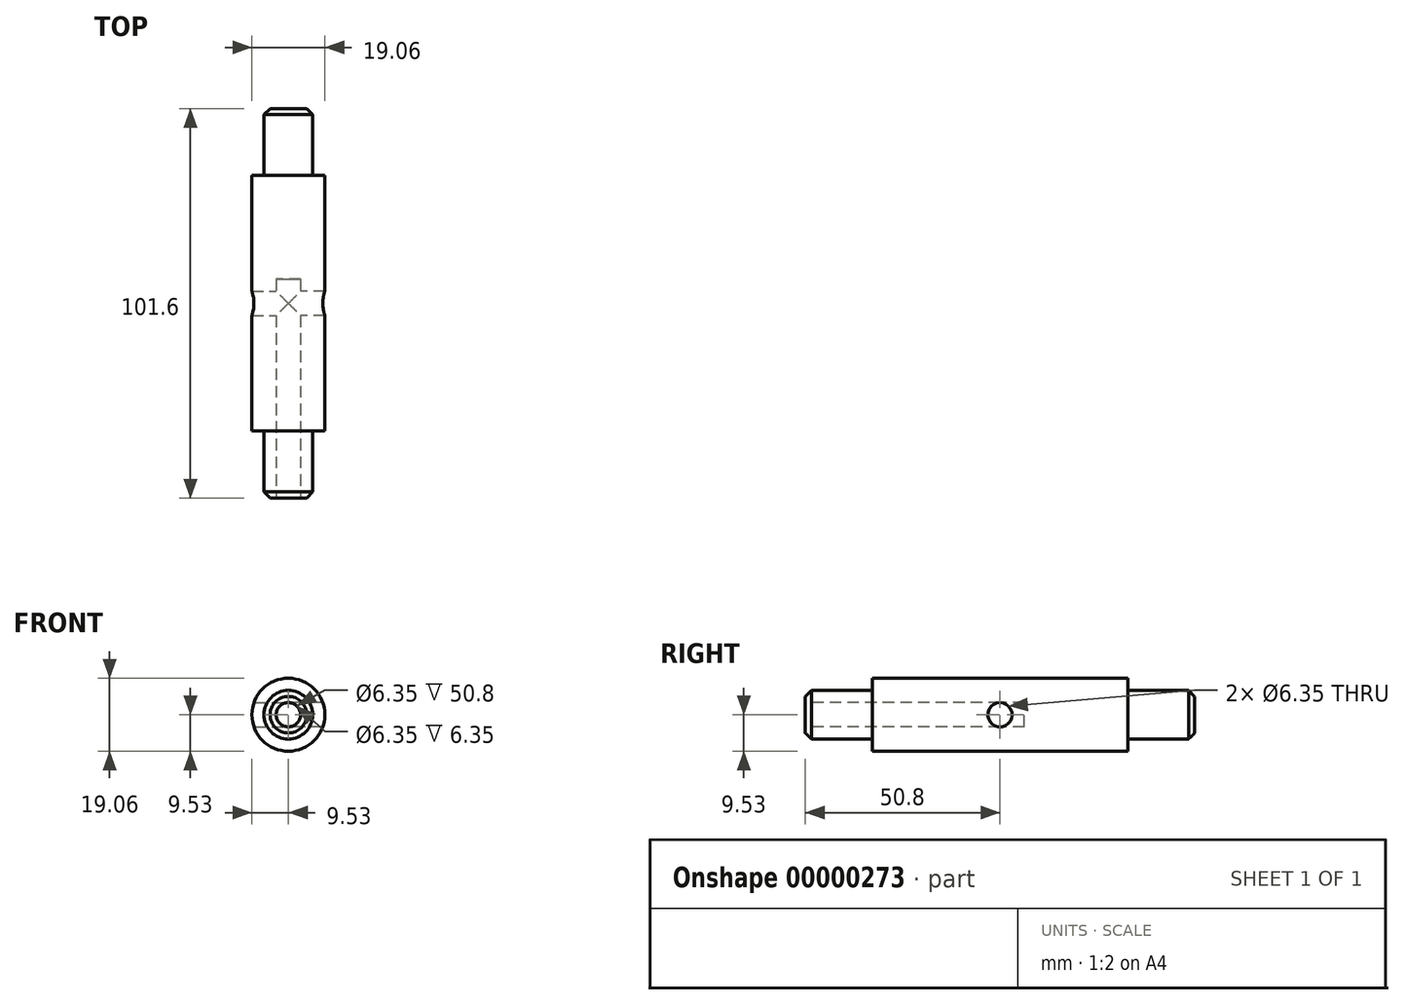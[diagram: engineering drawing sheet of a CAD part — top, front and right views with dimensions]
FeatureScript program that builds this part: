
annotation { "Feature Type Name" : "Feature", "Feature Type Description" : "" }
export const myFeature = defineFeature(function(context is Context, id is Id, definition is map)
    precondition{}
    {
        {
            var Q0;
            Q0=qCreatedBy(makeId("Front.planeOp"),FACE);
            var sketch = newSketch(context, id + "F0", { "sketchPlane" : qUnion([Q0])});
            skCircle(sketch, "E0", {"center": v(0, 0) * mm, "radius": 6.35 * mm});
            skSolve(sketch);
        }
        {
            var Q0;
            Q0=makeQuery(id+"F0.imprint","IMPRINT",FACE,{"disambiguationData":[TD([[makeQuery(id+"F0.imprint","IMPRINT",EDGE,{"derivedFrom":sQuery(id+"F0.wireOp",EDGE,"E0")}),1.0]])]});
            extrude(context, id + "F1", {"entities" : qUnion([Q0]), "depth" : 17.46 * mm});
        }
        {
            var Q0;
            Q0=makeQuery(id+"F1.opExtrude","CAP_FACE",FACE,{"disambiguationData":[OSD([sQuery(id+"F0.wireOp",EDGE,"E0")])],"isStart":false});
            var sketch = newSketch(context, id + "F2", { "sketchPlane" : qUnion([Q0])});
            skCircle(sketch, "E1", {"center": v(0, 0) * mm, "radius": 9.53 * mm});
            skSolve(sketch);
        }
        {
            var Q0;
            {var subQ0=makeQuery(id+"F2.imprint","IMPRINT",EDGE,{"derivedFrom":makeQuery(id+"F1.opExtrude","CAP_EDGE",EDGE,{"disambiguationData":[OSD([sQuery(id+"F0.wireOp",EDGE,"E0")])],"isStart":false})});Q0=qUnion([makeQuery(id+"F2.imprint","IMPRINT",FACE,{"disambiguationData":[TD([[makeQuery(id+"F2.imprint","IMPRINT",EDGE,{"derivedFrom":sQuery(id+"F2.wireOp",EDGE,"E1")}),1.0]])]}),makeQuery(id+"F2.imprint","IMPRINT",FACE,{"disambiguationData":[TD([[subQ0,1.0]])]})]);}
            extrude(context, id + "F3", {"entities" : qUnion([Q0]), "operationType" : NewBodyOperationType.ADD, "depth" : 66.67 * mm});
        }
        {
            var Q0;
            Q0=makeQuery(id+"F3.opExtrude","CAP_FACE",FACE,{"disambiguationData":[OSD([sQuery(id+"F2.wireOp",EDGE,"E1")])],"isStart":false});
            var sketch = newSketch(context, id + "F4", { "sketchPlane" : qUnion([Q0])});
            skCircle(sketch, "E2", {"center": v(0, 0) * mm, "radius": 6.35 * mm});
            skSolve(sketch);
        }
        {
            var Q0;
            Q0=makeQuery(id+"F4.imprint","IMPRINT",FACE,{"disambiguationData":[TD([[makeQuery(id+"F4.imprint","IMPRINT",EDGE,{"derivedFrom":sQuery(id+"F4.wireOp",EDGE,"E2")}),1.0]])]});
            extrude(context, id + "F5", {"entities" : qUnion([Q0]), "operationType" : NewBodyOperationType.ADD, "depth" : 17.46 * mm});
        }
        {
            var Q0;
            Q0=makeQuery(id+"F5.opExtrude","CAP_EDGE",EDGE,{"disambiguationData":[OSD([sQuery(id+"F4.wireOp",EDGE,"E2")])],"isStart":false});
            var Q1;
            Q1=makeQuery(id+"F1.opExtrude","CAP_EDGE",EDGE,{"disambiguationData":[OSD([sQuery(id+"F0.wireOp",EDGE,"E0")])],"isStart":true});
            chamfer(context, id + "F6", {"entities" : qUnion([Q0, Q1]), "width" : 1.59 * mm, "tangentPropagation" : true});
        }
        {
            var Q0;
            Q0=makeQuery(id+"F5.opExtrude","CAP_FACE",FACE,{"disambiguationData":[OSD([sQuery(id+"F4.wireOp",EDGE,"E2")])],"isStart":false});
            var sketch = newSketch(context, id + "F7", { "sketchPlane" : qUnion([Q0])});
            skCircle(sketch, "E3", {"center": v(0, 0) * mm, "radius": 3.18 * mm});
            skSolve(sketch);
        }
        {
            var Q0;
            Q0=makeQuery(id+"F7.imprint","IMPRINT",FACE,{"disambiguationData":[TD([[makeQuery(id+"F7.imprint","IMPRINT",EDGE,{"derivedFrom":sQuery(id+"F7.wireOp",EDGE,"E3")}),1.0]])]});
            extrude(context, id + "F8", {"entities" : qUnion([Q0]), "operationType" : NewBodyOperationType.REMOVE, "oppositeDirection" : true, "depth" : 57.15 * mm});
        }
        {
            var Q0;
            Q0=qCreatedBy(makeId("Right.planeOp"),FACE);
            var sketch = newSketch(context, id + "F9", { "sketchPlane" : qUnion([Q0])});
            skCircle(sketch, "E4", {"center": v(-50.8, 0) * mm, "radius": 3.18 * mm});
            skSolve(sketch);
        }
        {
            var Q0;
            Q0=makeQuery(id+"F9.imprint","IMPRINT",FACE,{"disambiguationData":[TD([[makeQuery(id+"F9.imprint","IMPRINT",EDGE,{"derivedFrom":sQuery(id+"F9.wireOp",EDGE,"E4")}),1.0]])]});
            var Q1;
            Q1=sQuery(id+"F9.wireOp",EDGE,"E4");
            extrude(context, id + "F10", {"entities" : qUnion([Q0]), "operationType" : NewBodyOperationType.REMOVE, "surfaceEntities" : qUnion([Q1]), "endBound" : BoundingType.THROUGH_ALL, "depth" : 25.4 * mm});
        }
        {
            var Q0;
            Q0=makeQuery(id+"F9.imprint","IMPRINT",FACE,{"disambiguationData":[TD([[makeQuery(id+"F9.imprint","IMPRINT",EDGE,{"derivedFrom":sQuery(id+"F9.wireOp",EDGE,"E4")}),1.0]])]});
            extrude(context, id + "F11", {"entities" : qUnion([Q0]), "operationType" : NewBodyOperationType.REMOVE, "endBound" : BoundingType.THROUGH_ALL, "oppositeDirection" : true, "depth" : 25.4 * mm});
        }
    });
